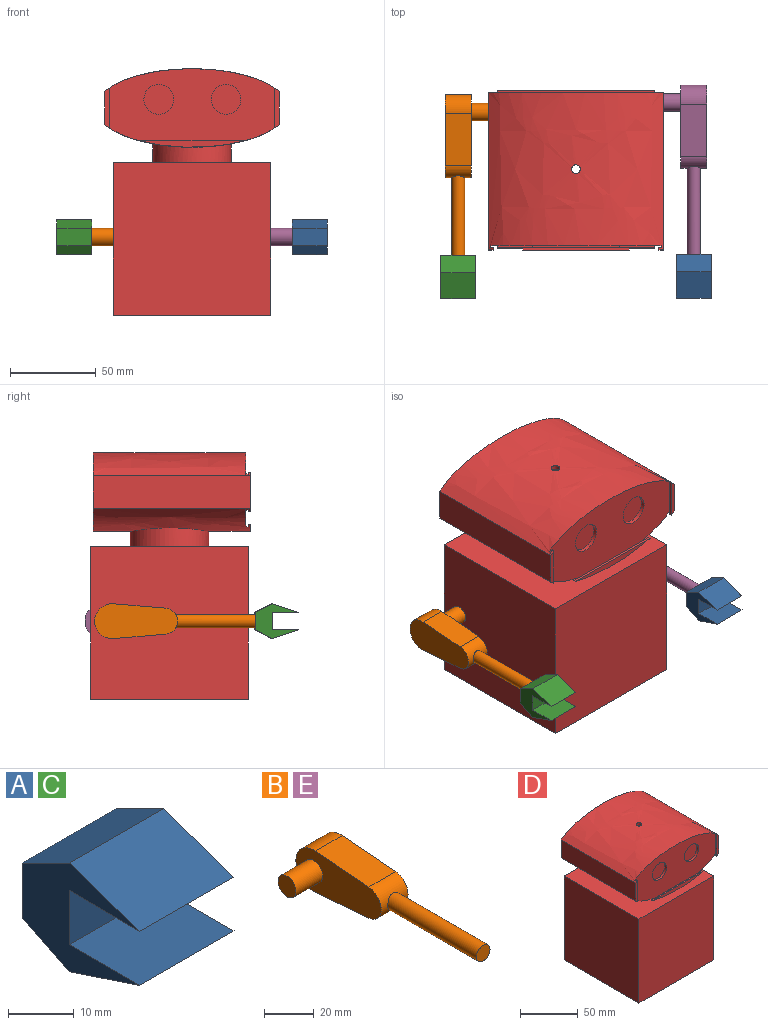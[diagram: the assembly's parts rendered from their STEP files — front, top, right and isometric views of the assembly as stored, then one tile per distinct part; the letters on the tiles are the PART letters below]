
ASSEMBLY  parts=5 mates=4
PART A: 12 faces, bbox 20.3x25.4x20.3 mm
  f0: plane 20.32x10.16mm, normal (0,0.45,0.89), area 230.8mm2, adj f1,f7,f8,f9
  f1: plane 20.32x15.24mm, normal (0,-0.32,0.95), area 327.1mm2, adj f0,f2,f8,f9
  f2: plane 20.32x15.24mm, normal (0,0.01,-1), area 309.7mm2, adj f1,f3,f8,f9
  f3: plane 20.32x10.16mm, normal (0,-1,0), area 206.5mm2, adj f2,f4,f8,f9
  f4: plane 20.32x15.24mm, normal (0,0,1), area 309.7mm2, adj f3,f5,f8,f9
  f5: plane 20.32x15.24mm, normal (0,-0.32,-0.95), area 326.4mm2, adj f4,f6,f8,f9
  f6: plane 20.32x10.16mm, normal (0,0.45,-0.89), area 230.8mm2, adj f5,f7,f8,f9
  f7: plane 20.32x10.16mm, normal (0,1,0), area 160.8mm2, adj f0,f6,f8,f9,f10
  f8: plane 25.4x20.32mm, normal (1,0,0), area 232.3mm2, adj f0,f1,f2,f3,f4,f5,f6,f7
  f9: plane 25.4x20.32mm, normal (-1,0,0), area 232.3mm2, adj f0,f1,f2,f3,f4,f5,f6,f7
  f10: cylinder r=3.81mm len=7.62mm, axis (0,1,0), area 121.6mm2, adj f7,f11
  f11: plane 7.62x7.62mm, normal (0,1,0), area 45.6mm2, adj f10
PART B: 10 faces, bbox 30.5x98.5x20.3 mm
  f0: cylinder r=7.62mm len=15.24mm, axis (-1,0,0), area 298.2mm2, adj f2,f3,f4,f5,f6
  f1: cylinder r=10.16mm len=20.32mm, axis (-1,0,0), area 512.3mm2, adj f2,f3,f4,f5
  f2: plane 30.27x15.24mm, normal (0,-0.08,1), area 462.9mm2, adj f0,f1,f4,f5
  f3: plane 30.27x15.24mm, normal (0,-0.08,-1), area 462.9mm2, adj f0,f1,f4,f5
  f4: plane 48.26x20.32mm, normal (1,0,0), area 797.2mm2, adj f0,f1,f2,f3
  f5: plane 48.26x20.32mm, normal (-1,0,0), area 716.1mm2, adj f0,f1,f2,f3,f8
  f6: cylinder r=3.81mm len=51.28mm, axis (0,1,0), area 1215.1mm2, adj f0,f7
  f7: plane 7.62x7.62mm, normal (0,-1,0), area 45.6mm2, adj f6
  f8: cylinder r=5.08mm len=15.24mm, axis (1,0,0), area 486.4mm2, adj f5,f9
  f9: plane 10.16x10.16mm, normal (-1,0,0), area 81.1mm2, adj f8
PART C: same geometry as A
PART D: 42 faces, bbox 101.6x92.7x143.5 mm
  f0: extruded ~96.52x83.82mm, area 8446.2mm2, adj f23,f24,f25,f26,f37
  f1: extruded ~101.6x91.44mm, area 8016mm2, adj f3,f4,f5,f6,f18,f19,f20,f21
  f2: extruded ~101.6x91.44mm, area 9498.8mm2, adj f3,f5,f6,f19,f20,f21,f28,f29
  f3: plane 23.05x2.54mm, normal (0,-1,0), area 53.7mm2, adj f1,f2,f20,f35
  f4: plane 61.78x3.81mm, normal (0,-1,0), area 159.7mm2, adj f1,f36
  f5: plane 23.05x1.27mm, normal (0,1,0), area 28.1mm2, adj f1,f2,f32,f34
  f6: plane 23.05x1.27mm, normal (0,1,0), area 28.1mm2, adj f1,f2,f30,f35
  f7: plane 91.44x91.44mm, normal (0,0,-1), area 903.2mm2, adj f8,f9,f10,f11,f13,f14,f15,f16
  f8: plane 91.44x88.9mm, normal (0,-1,0), area 8129mm2, adj f7,f9,f11,f12
  f9: plane 91.44x88.9mm, normal (1,0,0), area 8129mm2, adj f7,f8,f10,f12
  f10: plane 91.44x88.9mm, normal (0,1,0), area 8129mm2, adj f7,f9,f11,f12
  f11: plane 91.44x88.9mm, normal (-1,0,0), area 8129mm2, adj f7,f8,f10,f12
  f12: plane 91.44x91.44mm, normal (0,0,1), area 6719.5mm2, adj f8,f9,f10,f11,f18
  f13: plane 86.36x86.36mm, normal (0,1,0), area 7458mm2, adj f7,f14,f16,f17
  f14: plane 86.36x86.36mm, normal (-1,0,0), area 7458mm2, adj f7,f13,f15,f17
  f15: plane 86.36x86.36mm, normal (0,-1,0), area 7458mm2, adj f7,f14,f16,f17
  f16: plane 86.36x86.36mm, normal (1,0,0), area 7458mm2, adj f7,f13,f15,f17
  f17: plane 86.36x86.36mm, normal (0,0,-1), area 6160.9mm2, adj f13,f14,f15,f16,f22
  f18: cylinder r=22.86mm len=45.72mm, axis (0,0,-1), area 1418.8mm2, adj f1,f12
  f19: plane 101.6x45.72mm, normal (0,1,0), area 3882.9mm2, adj f1,f2,f20,f21
  f20: plane 91.44x19.05mm, normal (-1,0,0), area 1741.6mm2, adj f1,f2,f3,f19
  f21: plane 91.44x19.05mm, normal (1,0,0), area 1741.6mm2, adj f1,f2,f19,f28
  f22: cylinder r=20.32mm len=40.64mm, axis (0,0,-1), area 1884.6mm2, adj f17,f27
  f23: plane 96.52x40.65mm, normal (0,-1,0), area 3263.9mm2, adj f0,f24,f25,f27
  f24: plane 83.82x16.7mm, normal (1,0,0), area 1399.6mm2, adj f0,f23,f26,f27
  f25: plane 83.82x16.7mm, normal (-1,0,0), area 1399.6mm2, adj f0,f23,f26,f27
  f26: plane 96.52x40.65mm, normal (0,1,0), area 3263.9mm2, adj f0,f24,f25,f27
  f27: extruded ~96.52x83.82mm, area 7165.3mm2, adj f22,f23,f24,f25,f26
  f28: plane 23.05x2.54mm, normal (0,-1,0), area 53.7mm2, adj f1,f2,f21,f34
  f29: plane 99.06x43.18mm, normal (0,-1,0), area 3273.8mm2, adj f1,f2,f30,f32,f33,f38,f40
  f30: plane 21.17x1.27mm, normal (1,0,0), area 26.9mm2, adj f1,f2,f6,f29
  f31: plane 61.78x1.27mm, normal (0,1,0), area 72mm2, adj f1,f33,f36
  f32: plane 21.17x1.27mm, normal (-1,0,0), area 26.9mm2, adj f1,f2,f5,f29
  f33: plane 51.2x1.27mm, normal (0,0,1), area 65mm2, adj f1,f29,f31
  f34: plane 23.05x1.27mm, normal (-1,0,0), area 29.3mm2, adj f1,f2,f5,f28
  f35: plane 23.05x1.27mm, normal (1,0,0), area 29.3mm2, adj f1,f2,f3,f6
  f36: plane 61.78x1.27mm, normal (0,0,1), area 78.5mm2, adj f1,f4,f31
  f37: cylinder r=2.54mm len=5.08mm, axis (0,0,1), area 40.5mm2, adj f0,f2
  f38: cylinder r=8.65mm len=17.3mm, axis (0,-1,0), area 124.3mm2, adj f29,f39
  f39: plane 17.3x17.3mm, normal (0,-1,0), area 235.1mm2, adj f38
  f40: cylinder r=8.65mm len=17.3mm, axis (0,-1,0), area 124.3mm2, adj f29,f41
  f41: plane 17.3x17.3mm, normal (0,-1,0), area 235.1mm2, adj f40
PART E: same geometry as B
PLACE A t=(58.42,-59.59,43.36)mm
PLACE B rot(axis=(0,1,0),180deg) t=(-60.96,26.32,45.45)mm
PLACE C rot(axis=(0,-1,0),180deg) t=(-58.42,-60.04,47.59)mm
PLACE D at identity fixed
PLACE E t=(60.96,31.85,45.5)mm
MATE planar D.f9 <-> E.f1  axis (1,0,0) through (45.72,0,44.45)mm
MATE fastened C.f10 <-> B.f6  axis (0,1,0) through (-68.58,-54.96,45.45)mm
MATE planar D.f11 <-> B.f1  axis (-1,0,0) through (-45.72,0,44.45)mm
MATE fastened E.f6 <-> A.f10  axis (0,-1,0) through (68.58,-49.43,45.5)mm
